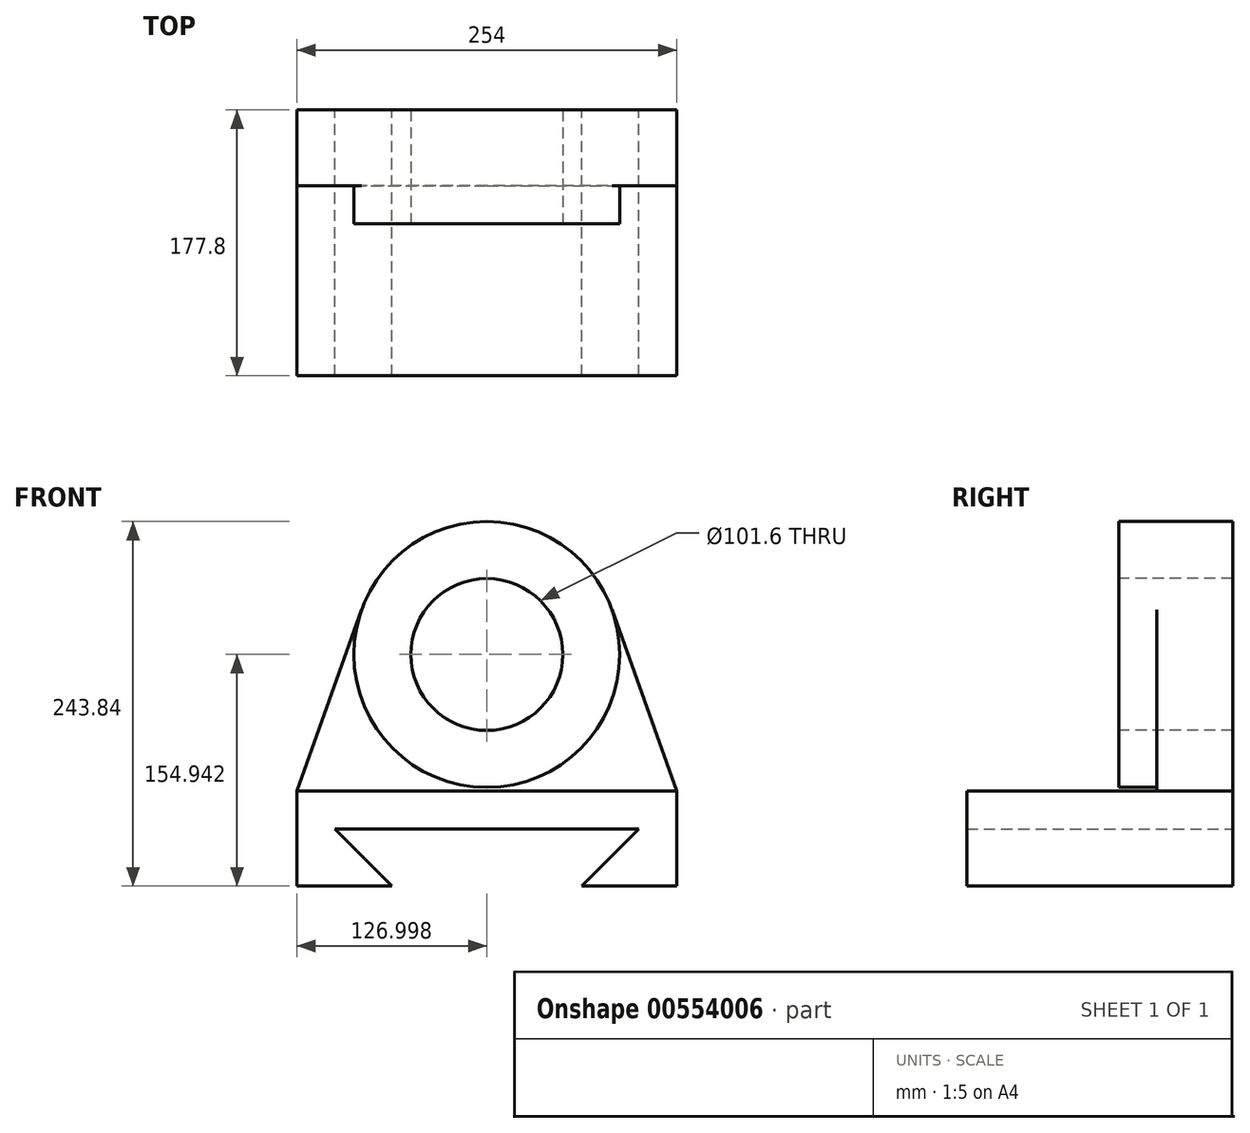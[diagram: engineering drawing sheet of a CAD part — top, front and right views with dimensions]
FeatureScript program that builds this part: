
annotation { "Feature Type Name" : "Feature", "Feature Type Description" : "" }
export const myFeature = defineFeature(function(context is Context, id is Id, definition is map)
    precondition{}
    {
        {
            var Q0;
            Q0=qCreatedBy(makeId("Front.planeOp"),FACE);
            var sketch = newSketch(context, id + "F0", { "sketchPlane" : qUnion([Q0])});
            skLineSegment(sketch, "E0", {"start": v(247.64, 138.9) * mm, "end": v(-6.36, 138.9) * mm});
            skCircle(sketch, "E1", {"center": v(120.64, 230.33) * mm, "radius": 50.8 * mm});
            skCircle(sketch, "E2", {"center": v(120.64, 230.33) * mm, "radius": 88.9 * mm});
            skLineSegment(sketch, "E3", {"start": v(-6.36, 138.9) * mm, "end": v(36.9, 260.2) * mm});
            skLineSegment(sketch, "E4", {"start": v(247.64, 138.9) * mm, "end": v(204.37, 260.2) * mm});
            skLineSegment(sketch, "E5", {"start": v(-6.36, 75.4) * mm, "end": v(-6.36, 138.9) * mm});
            skLineSegment(sketch, "E6", {"start": v(247.64, 75.4) * mm, "end": v(247.64, 138.9) * mm});
            skLineSegment(sketch, "E7", {"start": v(247.64, 75.4) * mm, "end": v(184.14, 75.4) * mm});
            skLineSegment(sketch, "E8", {"start": v(184.14, 75.4) * mm, "end": v(222.24, 113.5) * mm});
            skLineSegment(sketch, "E9", {"start": v(222.24, 113.5) * mm, "end": v(19.04, 113.5) * mm});
            skLineSegment(sketch, "E10", {"start": v(19.04, 113.5) * mm, "end": v(57.14, 75.4) * mm});
            skLineSegment(sketch, "E11", {"start": v(57.14, 75.4) * mm, "end": v(-6.36, 75.4) * mm});
            skSolve(sketch);
        }
        {
            var Q0;
            Q0=makeQuery(id+"F0.imprint","IMPRINT",FACE,{"disambiguationData":[TD([[makeQuery(id+"F0.imprint","IMPRINT",EDGE,{"derivedFrom":sQuery(id+"F0.wireOp",EDGE,"E0")}),1.0]])]});
            extrude(context, id + "F1", {"entities" : qUnion([Q0]), "depth" : 127 * mm, "offsetDistance" : 25.4 * mm});
        }
        {
            var Q0;
            Q0=makeQuery(id+"F0.imprint","IMPRINT",FACE,{"disambiguationData":[TD([[makeQuery(id+"F0.imprint","IMPRINT",EDGE,{"derivedFrom":sQuery(id+"F0.wireOp",EDGE,"E0")}),-1.0]])]});
            var Q1;
            Q1=makeQuery(id+"F0.imprint","IMPRINT",FACE,{"disambiguationData":[TD([[makeQuery(id+"F0.imprint","IMPRINT",EDGE,{"derivedFrom":sQuery(id+"F0.wireOp",EDGE,"E1")}),-1.0]])]});
            var Q2;
            Q2=makeQuery(id+"F0.imprint","IMPRINT",FACE,{"disambiguationData":[TD([[makeQuery(id+"F0.imprint","IMPRINT",EDGE,{"derivedFrom":sQuery(id+"F0.wireOp",EDGE,"E0")}),1.0]])]});
            extrude(context, id + "F2", {"entities" : qUnion([Q0, Q1, Q2]), "operationType" : NewBodyOperationType.ADD, "oppositeDirection" : true, "depth" : 50.8 * mm, "offsetDistance" : 25.4 * mm});
        }
        {
            var Q0;
            Q0=makeQuery(id+"F0.imprint","IMPRINT",FACE,{"disambiguationData":[TD([[makeQuery(id+"F0.imprint","IMPRINT",EDGE,{"derivedFrom":sQuery(id+"F0.wireOp",EDGE,"E1")}),-1.0]])]});
            extrude(context, id + "F3", {"entities" : qUnion([Q0]), "operationType" : NewBodyOperationType.ADD, "depth" : 25.4 * mm, "offsetDistance" : 25.4 * mm});
        }
    });
